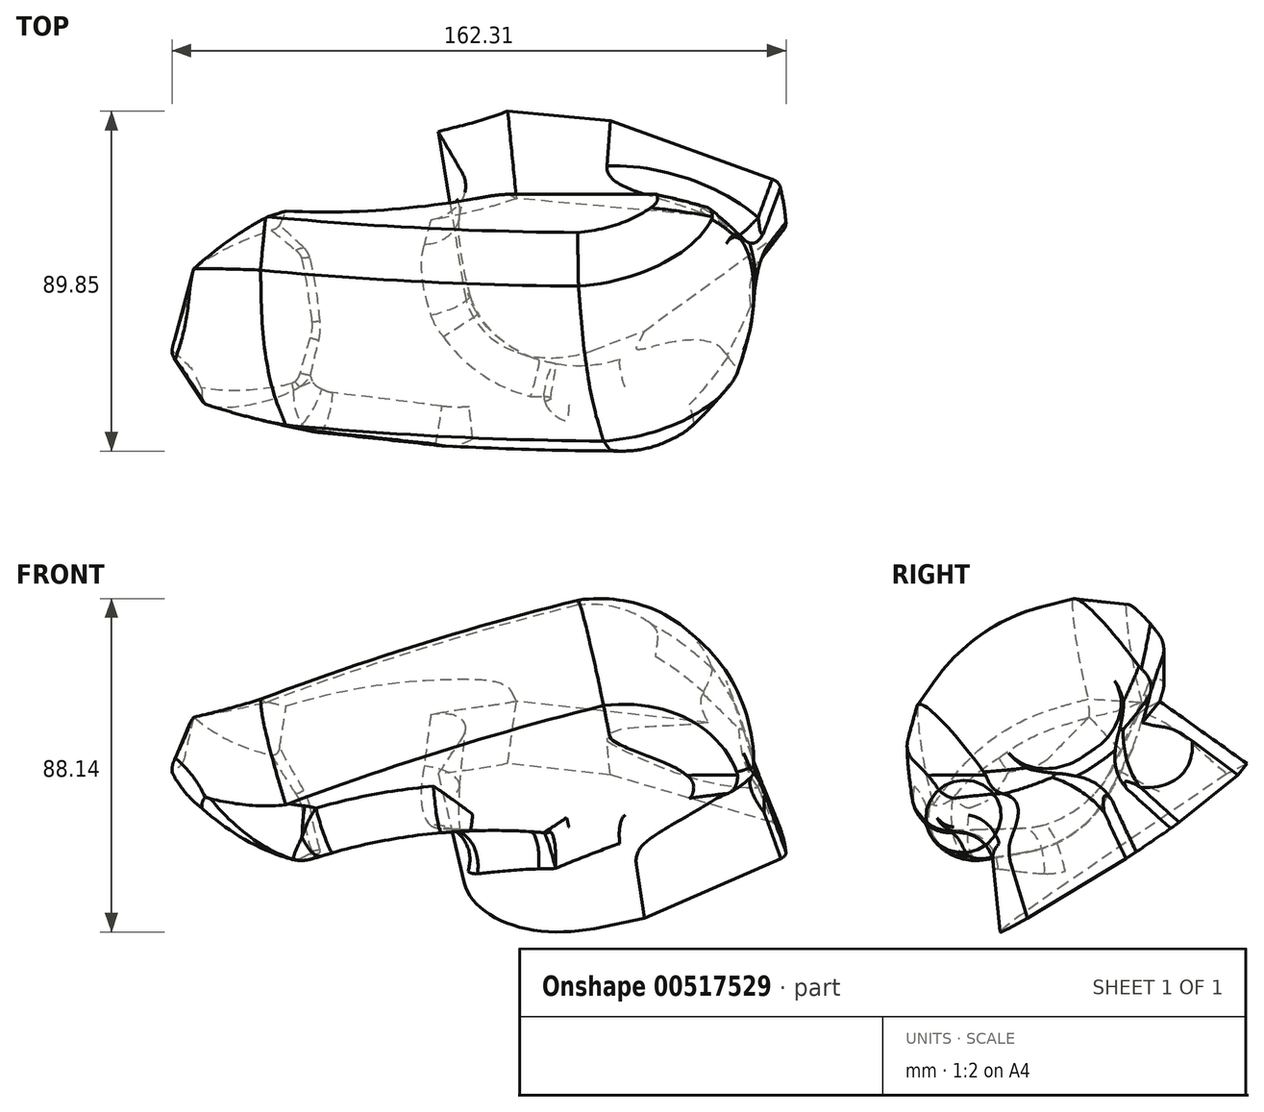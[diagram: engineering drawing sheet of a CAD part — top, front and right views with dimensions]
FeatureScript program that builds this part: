
annotation { "Feature Type Name" : "Feature", "Feature Type Description" : "" }
export const myFeature = defineFeature(function(context is Context, id is Id, definition is map)
    precondition{}
    {
        {
            var Q0;
            Q0=qCreatedBy(makeId("Front.planeOp"),FACE);
            var sketch = newSketch(context, id + "F0", { "sketchPlane" : qUnion([Q0])});
            skArc(sketch, "E0", {"start": v(39.04, 44.79) * mm, "mid": v(-4.05, 32.33) * mm, "end": v(-46.15, 16.82) * mm});
            skArc(sketch, "E1", {"start": v(-36.76, -19.76) * mm, "mid": v(-31.27, -20.86) * mm, "end": v(-25.67, -21) * mm});
            skArc(sketch, "E2", {"start": v(17.25, -16.9) * mm, "mid": v(-4.42, -16.77) * mm, "end": v(-25.67, -21) * mm});
            skArc(sketch, "E3", {"start": v(-68, -2) * mm, "mid": v(-48.8, -15.86) * mm, "end": v(-25.67, -21) * mm});
            skArc(sketch, "E4", {"start": v(88.24, 0) * mm, "mid": v(73.95, 33.71) * mm, "end": v(39.04, 44.79) * mm});
            skArc(sketch, "E5", {"start": v(88.24, 0) * mm, "mid": v(86.09, -26.94) * mm, "end": v(88.24, -53.88) * mm});
            skArc(sketch, "E6", {"start": v(25.94, -54.42) * mm, "mid": v(26.86, -34.44) * mm, "end": v(17.25, -16.9) * mm});
            skLineSegment(sketch, "E7", {"start": v(25.94, -54.42) * mm, "end": v(88.24, -53.88) * mm});
            skArc(sketch, "E8", {"start": v(89.31, 54.42) * mm, "mid": v(62.07, 56.05) * mm, "end": v(43.59, 35.97) * mm, "construction": true});
            skArc(sketch, "E9", {"start": v(75.94, 13.5) * mm, "mid": v(92.5, 30.73) * mm, "end": v(89.31, 54.42) * mm, "construction": true});
            skArc(sketch, "E10", {"start": v(75.94, 13.5) * mm, "mid": v(62.88, 29.22) * mm, "end": v(43.59, 35.97) * mm, "construction": true});
            skLineSegment(sketch, "E11", {"start": v(17.25, -16.9) * mm, "end": v(88.24, 0) * mm});
            skPoint(sketch, "E12.orphan", {"position": v(-57.22, -2) * mm});
            skArc(sketch, "E13", {"start": v(-66.55, 11.44) * mm, "mid": v(-69.79, 4.99) * mm, "end": v(-68, -2) * mm});
            skArc(sketch, "E14", {"start": v(-66.55, 11.44) * mm, "mid": v(-56.28, 13.86) * mm, "end": v(-46.15, 16.82) * mm});
            skPoint(sketch, "E15.orphan", {"position": v(-57.22, 12.17) * mm});
            skPoint(sketch, "E16.start.orphan", {"position": v(-73.67, 12.17) * mm});
            skSolve(sketch);
        }
        {
            var Q0;
            Q0=makeQuery(id+"F0.imprint","IMPRINT",FACE,{"disambiguationData":[TD([[makeQuery(id+"F0.imprint","IMPRINT",EDGE,{"derivedFrom":sQuery(id+"F0.wireOp",EDGE,"E0")}),1.0]])]});
            extrude(context, id + "F1", {"entities" : qUnion([Q0]), "depth" : 25 * mm, "offsetDistance" : 25 * mm, "hasDraft" : true, "draftAngle" : 20 * degree, "draftPullDirection" : true});
        }
        {
            var Q0;
            Q0=makeQuery(id+"F1.opExtrude","CAP_FACE",FACE,{"disambiguationData":[OSD([sQuery(id+"F0.wireOp",EDGE,"E0"),sQuery(id+"F0.wireOp",EDGE,"p0q2MJaU-Hp2x-FXpI-a7RR-1GAnmMj39aOJ"),sQuery(id+"F0.wireOp",EDGE,"E2"),sQuery(id+"F0.wireOp",EDGE,"1ELn8xg3-YaXG-rdAX-tHKt-Tl8SfEgkcqDu"),sQuery(id+"F0.wireOp",EDGE,"E3"),sQuery(id+"F0.wireOp",EDGE,"E4"),sQuery(id+"F0.wireOp",EDGE,"E11")])],"isStart":false});
            extrude(context, id + "F2", {"entities" : qUnion([Q0]), "operationType" : NewBodyOperationType.ADD, "depth" : 10.9 * mm, "offsetDistance" : 25 * mm, "hasDraft" : true, "draftAngle" : 40 * degree, "draftPullDirection" : true});
        }
        {
            var Q0;
            Q0=makeQuery(id+"F1.opExtrude","CAP_FACE",FACE,{"disambiguationData":[OSD([sQuery(id+"F0.wireOp",EDGE,"E0"),sQuery(id+"F0.wireOp",EDGE,"p0q2MJaU-Hp2x-FXpI-a7RR-1GAnmMj39aOJ"),sQuery(id+"F0.wireOp",EDGE,"E2"),sQuery(id+"F0.wireOp",EDGE,"1ELn8xg3-YaXG-rdAX-tHKt-Tl8SfEgkcqDu"),sQuery(id+"F0.wireOp",EDGE,"E3"),sQuery(id+"F0.wireOp",EDGE,"E4"),sQuery(id+"F0.wireOp",EDGE,"E11")])],"isStart":true});
            var sketch = newSketch(context, id + "F3", { "sketchPlane" : qUnion([Q0])});
            skArc(sketch, "E17", {"start": v(-39.04, 44.79) * mm, "mid": v(-14, -32.04) * mm, "end": v(62.82, -7) * mm});
            skSolve(sketch);
        }
        {
            var Q0;
            Q0 = qSketchRegion(id + "F3", true);
            var Q1;
            {var subQ0=sQuery(id+"F3.wireOp",EDGE,"E17");Q1=makeQuery(id+"F3.imprint","IMPRINT",FACE,{"disambiguationData":[TD([[makeQuery(id+"F3.imprint","IMPRINT",EDGE,{"derivedFrom":subQ0}),1.0]])]});}
            extrude(context, id + "F4", {"entities" : qUnion([Q0, Q1]), "operationType" : NewBodyOperationType.REMOVE, "oppositeDirection" : true, "depth" : 25 * mm, "offsetDistance" : 25 * mm});
        }
        {
            var Q0;
            Q0=makeQuery(id+"F1.opExtrude","CAP_FACE",FACE,{"disambiguationData":[OSD([sQuery(id+"F0.wireOp",EDGE,"E0"),sQuery(id+"F0.wireOp",EDGE,"p0q2MJaU-Hp2x-FXpI-a7RR-1GAnmMj39aOJ"),sQuery(id+"F0.wireOp",EDGE,"E2"),sQuery(id+"F0.wireOp",EDGE,"1ELn8xg3-YaXG-rdAX-tHKt-Tl8SfEgkcqDu"),sQuery(id+"F0.wireOp",EDGE,"E3"),sQuery(id+"F0.wireOp",EDGE,"E4"),sQuery(id+"F0.wireOp",EDGE,"E11")])],"isStart":true});
            var sketch = newSketch(context, id + "F5", { "sketchPlane" : qUnion([Q0])});
            skLineSegment(sketch, "E18", {"start": v(-17.25, -16.9) * mm, "end": v(-17.25, 0) * mm});
            skLineSegment(sketch, "E19", {"start": v(-17.25, 0) * mm, "end": v(-88.24, 0) * mm});
            skSolve(sketch);
        }
        {
            var Q0;
            Q0 = qSketchRegion(id + "F5", true);
            var Q1;
            Q1=makeQuery(id+"F5.imprint","IMPRINT",FACE,{"disambiguationData":[TD([[makeQuery(id+"F5.imprint","IMPRINT",EDGE,{"derivedFrom":sQuery(id+"F5.wireOp",EDGE,"E18")}),1.0]])]});
            extrude(context, id + "F6", {"entities" : qUnion([Q0, Q1]), "operationType" : NewBodyOperationType.REMOVE, "oppositeDirection" : true, "depth" : 76.9 * mm, "offsetDistance" : 25 * mm});
        }
        {
            var Q0;
            {var subQ0=sQuery(id+"F0.wireOp",EDGE,"E2");Q0=makeQuery(id+"F2.boolean.opBoolean","MERGE",EDGE,{"derivedFrom":[makeQuery(id+"F1.opExtrude","CAP_EDGE",EDGE,{"disambiguationData":[OSD([subQ0])],"isStart":false}),makeQuery(id+"F2.opExtrude","CAP_EDGE",EDGE,{"disambiguationData":[OSD([subQ0])],"isStart":true})]});}
            fillet(context, id + "F7", {"entities" : qUnion([Q0]), "radius" : 363 * mm, "tangentPropagation" : true, "allowEdgeOverflow" : false});
        }
        {
            var Q0;
            Q0=makeQuery(id+"F1.opExtrude","SWEPT_BODY",BODY,{"disambiguationData":[OSD([sQuery(id+"F0.wireOp",EDGE,"E0"),sQuery(id+"F0.wireOp",EDGE,"p0q2MJaU-Hp2x-FXpI-a7RR-1GAnmMj39aOJ"),sQuery(id+"F0.wireOp",EDGE,"E2"),sQuery(id+"F0.wireOp",EDGE,"1ELn8xg3-YaXG-rdAX-tHKt-Tl8SfEgkcqDu"),sQuery(id+"F0.wireOp",EDGE,"E3"),sQuery(id+"F0.wireOp",EDGE,"E4"),sQuery(id+"F0.wireOp",EDGE,"E11")])]});
            var Q1;
            Q1=qCreatedBy(makeId("Front.planeOp"),FACE);
            mirror(context, id + "F8", {"operationType" : NewBodyOperationType.ADD, "entities" : qUnion([Q0]), "mirrorPlane" : qUnion([Q1])});
        }
        {
            var Q0;
            {var subQ0=makeQuery(id+"F1.opExtrude","CAP_EDGE",EDGE,{"disambiguationData":[OSD([sQuery(id+"F0.wireOp",EDGE,"E0")])],"isStart":true});Q0=makeQuery(id+"F8.boolean.opBoolean","MERGE",EDGE,{"derivedFrom":[subQ0,makeQuery(id+"F8.opPattern","COPY",EDGE,{"derivedFrom":subQ0,"instanceName":"1"})]});}
            var Q1;
            {var subQ0=makeQuery(id+"F1.opExtrude","CAP_EDGE",EDGE,{"disambiguationData":[OSD([sQuery(id+"F0.wireOp",EDGE,"E4")])],"isStart":true});Q1=makeQuery(id+"F8.boolean.opBoolean","MERGE",EDGE,{"derivedFrom":[subQ0,makeQuery(id+"F8.opPattern","COPY",EDGE,{"derivedFrom":subQ0,"instanceName":"1"})]});}
            fillet(context, id + "F9", {"entities" : qUnion([Q0, Q1]), "radius" : 50 * mm, "tangentPropagation" : true, "allowEdgeOverflow" : false});
        }
        {
            var Q0;
            Q0=makeQuery(id+"F2.opExtrude","CAP_EDGE",EDGE,{"disambiguationData":[OSD([sQuery(id+"F0.wireOp",EDGE,"E3")])],"isStart":false});
            fillet(context, id + "F10", {"entities" : qUnion([Q0]), "radius" : 10 * mm, "tangentPropagation" : true, "allowEdgeOverflow" : false});
        }
        {
            var Q0;
            Q0=makeQuery(id+"F10.opFillet","BLEND_EDGE",EDGE,{"blendedFrom":[makeQuery(id+"F2.opExtrude","CAP_EDGE",EDGE,{"disambiguationData":[OSD([sQuery(id+"F0.wireOp",EDGE,"E3")])],"isStart":false}),makeQuery(id+"F2.opExtrude","SWEPT_FACE",FACE,{"disambiguationData":[OSD([sQuery(id+"F0.wireOp",EDGE,"E0")])]})],"blendedInto":[makeQuery(id+"F2.opExtrude","SWEPT_FACE",FACE,{"disambiguationData":[OSD([sQuery(id+"F0.wireOp",EDGE,"E0")])]})]});
            var Q1;
            Q1=makeQuery(id+"F10.opFillet","BLEND_EDGE",EDGE,{"blendedFrom":[makeQuery(id+"F2.opExtrude","CAP_EDGE",EDGE,{"disambiguationData":[OSD([sQuery(id+"F0.wireOp",EDGE,"E3")])],"isStart":false}),makeQuery(id+"F2.opExtrude","SWEPT_FACE",FACE,{"disambiguationData":[OSD([sQuery(id+"F0.wireOp",EDGE,"E14")])]})],"blendedInto":[makeQuery(id+"F2.opExtrude","SWEPT_FACE",FACE,{"disambiguationData":[OSD([sQuery(id+"F0.wireOp",EDGE,"E14")])]})]});
            fillet(context, id + "F11", {"entities" : qUnion([Q0, Q1]), "radius" : 12.2 * mm, "tangentPropagation" : true, "allowEdgeOverflow" : false});
        }
        {
            var Q0;
            {var subQ0=sQuery(id+"F0.wireOp",EDGE,"E2");Q0=makeQuery(id+"F7.opFillet","BLEND_EDGE",EDGE,{"blendedFrom":[makeQuery(id+"F2.boolean.opBoolean","MERGE",EDGE,{"derivedFrom":[makeQuery(id+"F1.opExtrude","CAP_EDGE",EDGE,{"disambiguationData":[OSD([subQ0])],"isStart":false}),makeQuery(id+"F2.opExtrude","CAP_EDGE",EDGE,{"disambiguationData":[OSD([subQ0])],"isStart":true})]}),makeQuery(id+"F2.opExtrude","SWEPT_FACE",FACE,{"disambiguationData":[OSD([sQuery(id+"F0.wireOp",EDGE,"E3")])]})],"blendedInto":[makeQuery(id+"F2.opExtrude","SWEPT_FACE",FACE,{"disambiguationData":[OSD([sQuery(id+"F0.wireOp",EDGE,"E3")])]})]});}
            var Q1;
            Q1=makeQuery(id+"F11.opFillet","BLEND_EDGE",EDGE,{"disambiguationData":[OD(1.0)],"blendedFrom":[makeQuery(id+"F2.opExtrude","SWEPT_EDGE",EDGE,{"disambiguationData":[OSD([sQuery(id+"F0.wireOp",EDGE,"E3"),sQuery(id+"F0.wireOp",EDGE,"E14")])]}),makeQuery(id+"F7.opFillet","BLEND_FACE",FACE,{"disambiguationData":[OSD([sQuery(id+"F0.wireOp",EDGE,"E2")])]})],"blendedInto":[makeQuery(id+"F7.opFillet","BLEND_FACE",FACE,{"disambiguationData":[OSD([sQuery(id+"F0.wireOp",EDGE,"E2")])]})]});
            fillet(context, id + "F12", {"entities" : qUnion([Q0, Q1]), "radius" : 10 * mm, "tangentPropagation" : true, "allowEdgeOverflow" : false});
        }
        {
            var Q0;
            {var subQ0=makeQuery(id+"F1.opExtrude","CAP_EDGE",EDGE,{"disambiguationData":[OSD([sQuery(id+"F0.wireOp",EDGE,"E3")])],"isStart":true});Q0=makeQuery(id+"F8.boolean.opBoolean","MERGE",EDGE,{"derivedFrom":[subQ0,makeQuery(id+"F8.opPattern","COPY",EDGE,{"derivedFrom":subQ0,"instanceName":"1"})]});}
            var Q1;
            {var subQ0=sQuery(id+"F0.wireOp",EDGE,"E2");var subQ1=makeQuery(id+"F7.opFillet","BLEND_EDGE",EDGE,{"blendedFrom":[makeQuery(id+"F2.boolean.opBoolean","MERGE",EDGE,{"derivedFrom":[makeQuery(id+"F1.opExtrude","CAP_EDGE",EDGE,{"disambiguationData":[OSD([subQ0])],"isStart":false}),makeQuery(id+"F2.opExtrude","CAP_EDGE",EDGE,{"disambiguationData":[OSD([subQ0])],"isStart":true})]}),makeQuery(id+"F1.opExtrude","CAP_FACE",FACE,{"disambiguationData":[OSD([sQuery(id+"F0.wireOp",EDGE,"E0"),subQ0,sQuery(id+"F0.wireOp",EDGE,"E3"),sQuery(id+"F0.wireOp",EDGE,"E4"),sQuery(id+"F0.wireOp",EDGE,"E11"),sQuery(id+"F0.wireOp",EDGE,"E13"),sQuery(id+"F0.wireOp",EDGE,"E14")])],"isStart":true})],"blendedInto":[makeQuery(id+"F1.opExtrude","CAP_FACE",FACE,{"disambiguationData":[OSD([sQuery(id+"F0.wireOp",EDGE,"E0"),subQ0,sQuery(id+"F0.wireOp",EDGE,"E3"),sQuery(id+"F0.wireOp",EDGE,"E4"),sQuery(id+"F0.wireOp",EDGE,"E11"),sQuery(id+"F0.wireOp",EDGE,"E13"),sQuery(id+"F0.wireOp",EDGE,"E14")])],"isStart":true})]});Q1=makeQuery(id+"F8.boolean.opBoolean","MERGE",EDGE,{"derivedFrom":[subQ1,makeQuery(id+"F8.opPattern","COPY",EDGE,{"derivedFrom":subQ1,"instanceName":"1"})]});}
            fillet(context, id + "F13", {"entities" : qUnion([Q0, Q1]), "radius" : 30 * mm, "tangentPropagation" : true, "allowEdgeOverflow" : false});
        }
        {
            var Q0;
            {var subQ0=sQuery(id+"F0.wireOp",EDGE,"E3");var subQ1=sQuery(id+"F0.wireOp",EDGE,"E2");var subQ2=makeQuery(id+"F7.opFillet","BLEND_EDGE",EDGE,{"blendedFrom":[makeQuery(id+"F2.boolean.opBoolean","MERGE",EDGE,{"derivedFrom":[makeQuery(id+"F1.opExtrude","CAP_EDGE",EDGE,{"disambiguationData":[OSD([subQ1])],"isStart":false}),makeQuery(id+"F2.opExtrude","CAP_EDGE",EDGE,{"disambiguationData":[OSD([subQ1])],"isStart":true})]}),makeQuery(id+"F1.opExtrude","CAP_FACE",FACE,{"disambiguationData":[OSD([sQuery(id+"F0.wireOp",EDGE,"E0"),subQ1,subQ0,sQuery(id+"F0.wireOp",EDGE,"E4"),sQuery(id+"F0.wireOp",EDGE,"E11"),sQuery(id+"F0.wireOp",EDGE,"E13"),sQuery(id+"F0.wireOp",EDGE,"E14")])],"isStart":true})],"blendedInto":[makeQuery(id+"F1.opExtrude","CAP_FACE",FACE,{"disambiguationData":[OSD([sQuery(id+"F0.wireOp",EDGE,"E0"),subQ1,subQ0,sQuery(id+"F0.wireOp",EDGE,"E4"),sQuery(id+"F0.wireOp",EDGE,"E11"),sQuery(id+"F0.wireOp",EDGE,"E13"),sQuery(id+"F0.wireOp",EDGE,"E14")])],"isStart":true})]});var subQ3=makeQuery(id+"F1.opExtrude","CAP_EDGE",EDGE,{"disambiguationData":[OSD([subQ0])],"isStart":true});Q0=makeQuery(id+"F13.opFillet","BLEND_EDGE",EDGE,{"blendedFrom":[makeQuery(id+"F8.boolean.opBoolean","MERGE",EDGE,{"derivedFrom":[subQ3,makeQuery(id+"F8.opPattern","COPY",EDGE,{"derivedFrom":subQ3,"instanceName":"1"})]}),makeQuery(id+"F8.boolean.opBoolean","MERGE",EDGE,{"derivedFrom":[subQ2,makeQuery(id+"F8.opPattern","COPY",EDGE,{"derivedFrom":subQ2,"instanceName":"1"})]})],"blendedInto":[]});}
            fillet(context, id + "F14", {"entities" : qUnion([Q0]), "radius" : 5 * mm, "tangentPropagation" : true, "allowEdgeOverflow" : false});
        }
        {
            var Q0;
            {var subQ0=makeQuery(id+"F6.boolean.opBoolean","COPY",FACE,{"derivedFrom":makeQuery(id+"F6.opExtrude","SWEPT_FACE",FACE,{"disambiguationData":[OSD([sQuery(id+"F5.wireOp",EDGE,"E19")])]})});Q0=makeQuery(id+"F8.boolean.opBoolean","MERGE",FACE,{"derivedFrom":[subQ0,makeQuery(id+"F8.opPattern","COPY",FACE,{"derivedFrom":subQ0,"instanceName":"1"})]});}
            extrude(context, id + "F15", {"entities" : qUnion([Q0]), "operationType" : NewBodyOperationType.ADD, "depth" : 26.6 * mm, "offsetDistance" : 25 * mm, "hasDraft" : true, "draftAngle" : 20 * degree});
        }
        {
            var Q0;
            {var subQ0=sQuery(id+"F5.wireOp",EDGE,"E19");var subQ1=sQuery(id+"F5.wireOp",EDGE,"E18");var subQ2=sQuery(id+"F0.wireOp",EDGE,"E2");Q0=makeQuery(id+"F15.opExtrude","SWEPT_EDGE",EDGE,{"disambiguationData":[OSD([subQ2,subQ1,subQ0]),TDD([makeQuery(id+"F7.opFillet","BLEND_VERTEX",VERTEX,{"blendedFrom":[makeQuery(id+"F2.boolean.opBoolean","MERGE",EDGE,{"derivedFrom":[makeQuery(id+"F1.opExtrude","CAP_EDGE",EDGE,{"disambiguationData":[OSD([subQ2])],"isStart":false}),makeQuery(id+"F2.opExtrude","CAP_EDGE",EDGE,{"disambiguationData":[OSD([subQ2])],"isStart":true})]}),makeQuery(id+"F6.boolean.opBoolean","COPY",FACE,{"derivedFrom":makeQuery(id+"F6.opExtrude","SWEPT_FACE",FACE,{"disambiguationData":[OSD([subQ1])]})}),makeQuery(id+"F6.boolean.opBoolean","COPY",FACE,{"derivedFrom":makeQuery(id+"F6.opExtrude","SWEPT_FACE",FACE,{"disambiguationData":[OSD([subQ0])]})})],"blendedInto":[makeQuery(id+"F6.boolean.opBoolean","COPY",FACE,{"derivedFrom":makeQuery(id+"F6.opExtrude","SWEPT_FACE",FACE,{"disambiguationData":[OSD([subQ1])]})}),makeQuery(id+"F6.boolean.opBoolean","COPY",FACE,{"derivedFrom":makeQuery(id+"F6.opExtrude","SWEPT_FACE",FACE,{"disambiguationData":[OSD([subQ0])]})})]})])]});}
            fillet(context, id + "F16", {"entities" : qUnion([Q0]), "radius" : 27.28 * mm, "tangentPropagation" : true, "allowEdgeOverflow" : false});
        }
        {
            var Q0;
            {var subQ0=sQuery(id+"F5.wireOp",EDGE,"E19");var subQ1=makeQuery(id+"F6.opExtrude","SWEPT_FACE",FACE,{"disambiguationData":[OSD([subQ0])]});var subQ2=sQuery(id+"F0.wireOp",EDGE,"E11");var subQ3=sQuery(id+"F5.wireOp",EDGE,"E18");var subQ4=sQuery(id+"F0.wireOp",EDGE,"E2");Q0=makeQuery(id+"F16.opFillet","BLEND_EDGE",EDGE,{"blendedFrom":[makeQuery(id+"F15.opExtrude","SWEPT_EDGE",EDGE,{"disambiguationData":[OSD([subQ4,subQ3,subQ0]),TDD([makeQuery(id+"F7.opFillet","BLEND_VERTEX",VERTEX,{"blendedFrom":[makeQuery(id+"F2.boolean.opBoolean","MERGE",EDGE,{"derivedFrom":[makeQuery(id+"F1.opExtrude","CAP_EDGE",EDGE,{"disambiguationData":[OSD([subQ4])],"isStart":false}),makeQuery(id+"F2.opExtrude","CAP_EDGE",EDGE,{"disambiguationData":[OSD([subQ4])],"isStart":true})]}),makeQuery(id+"F6.boolean.opBoolean","COPY",FACE,{"derivedFrom":makeQuery(id+"F6.opExtrude","SWEPT_FACE",FACE,{"disambiguationData":[OSD([subQ3])]})}),makeQuery(id+"F6.boolean.opBoolean","COPY",FACE,{"derivedFrom":subQ1})],"blendedInto":[makeQuery(id+"F6.boolean.opBoolean","COPY",FACE,{"derivedFrom":makeQuery(id+"F6.opExtrude","SWEPT_FACE",FACE,{"disambiguationData":[OSD([subQ3])]})}),makeQuery(id+"F6.boolean.opBoolean","COPY",FACE,{"derivedFrom":subQ1})]})])]}),makeQuery(id+"F15.opExtrude","SWEPT_FACE",FACE,{"disambiguationData":[OSD([subQ2,subQ0]),TDD([makeQuery(id+"F6.boolean.opBoolean","INTERSECT",EDGE,{"derivedFrom":[makeQuery(id+"F2.opExtrude","SWEPT_FACE",FACE,{"disambiguationData":[OSD([subQ2])]}),subQ1]})])]})],"blendedInto":[makeQuery(id+"F15.opExtrude","SWEPT_FACE",FACE,{"disambiguationData":[OSD([subQ2,subQ0]),TDD([makeQuery(id+"F6.boolean.opBoolean","INTERSECT",EDGE,{"derivedFrom":[makeQuery(id+"F2.opExtrude","SWEPT_FACE",FACE,{"disambiguationData":[OSD([subQ2])]}),subQ1]})])]})]});}
            fillet(context, id + "F17", {"entities" : qUnion([Q0]), "radius" : 26.35 * mm, "tangentPropagation" : true, "allowEdgeOverflow" : false});
        }
        {
            var Q0;
            {var subQ0=sQuery(id+"F5.wireOp",EDGE,"E19");var subQ1=makeQuery(id+"F6.opExtrude","SWEPT_FACE",FACE,{"disambiguationData":[OSD([subQ0])]});var subQ2=makeQuery(id+"F6.boolean.opBoolean","COPY",FACE,{"derivedFrom":subQ1});var subQ3=sQuery(id+"F0.wireOp",EDGE,"E11");var subQ4=sQuery(id+"F0.wireOp",EDGE,"E4");var subQ5=makeQuery(id+"F1.opExtrude","CAP_EDGE",EDGE,{"disambiguationData":[OSD([subQ4])],"isStart":true});Q0=makeQuery(id+"F15.opExtrude","SWEPT_EDGE",EDGE,{"disambiguationData":[OSD([subQ4,subQ3,subQ0]),TDD([makeQuery(id+"F9.opFillet","BLEND_VERTEX",VERTEX,{"blendedFrom":[makeQuery(id+"F8.boolean.opBoolean","MERGE",EDGE,{"derivedFrom":[subQ5,makeQuery(id+"F8.opPattern","COPY",EDGE,{"derivedFrom":subQ5,"instanceName":"1"})]}),makeQuery(id+"F6.boolean.opBoolean","SPLIT",FACE,{"disambiguationData":[TD([makeQuery(id+"F1.opExtrude","SWEPT_FACE",FACE,{"disambiguationData":[OSD([subQ4])]})])],"derivedFrom":makeQuery(id+"F1.opExtrude","SWEPT_FACE",FACE,{"disambiguationData":[OSD([subQ3])]})}),makeQuery(id+"F8.boolean.opBoolean","MERGE",FACE,{"derivedFrom":[subQ2,makeQuery(id+"F8.opPattern","COPY",FACE,{"derivedFrom":subQ2,"instanceName":"1"})]})],"blendedInto":[makeQuery(id+"F6.boolean.opBoolean","SPLIT",FACE,{"disambiguationData":[TD([makeQuery(id+"F1.opExtrude","SWEPT_FACE",FACE,{"disambiguationData":[OSD([subQ4])]})])],"derivedFrom":makeQuery(id+"F1.opExtrude","SWEPT_FACE",FACE,{"disambiguationData":[OSD([subQ3])]})}),makeQuery(id+"F8.boolean.opBoolean","MERGE",FACE,{"derivedFrom":[subQ2,makeQuery(id+"F8.opPattern","COPY",FACE,{"derivedFrom":subQ2,"instanceName":"1"})]})]})])]});}
            var Q1;
            {var subQ0=sQuery(id+"F5.wireOp",EDGE,"E19");var subQ1=makeQuery(id+"F6.opExtrude","SWEPT_FACE",FACE,{"disambiguationData":[OSD([subQ0])]});var subQ2=makeQuery(id+"F6.boolean.opBoolean","COPY",FACE,{"derivedFrom":subQ1});var subQ3=sQuery(id+"F0.wireOp",EDGE,"E11");var subQ4=sQuery(id+"F0.wireOp",EDGE,"E4");var subQ5=makeQuery(id+"F1.opExtrude","CAP_EDGE",EDGE,{"disambiguationData":[OSD([subQ4])],"isStart":true});Q1=makeQuery(id+"F15.opExtrude","SWEPT_EDGE",EDGE,{"disambiguationData":[OSD([subQ4,subQ3,subQ0]),TDD([makeQuery(id+"F9.opFillet","BLEND_VERTEX",VERTEX,{"blendedFrom":[makeQuery(id+"F8.boolean.opBoolean","MERGE",EDGE,{"derivedFrom":[subQ5,makeQuery(id+"F8.opPattern","COPY",EDGE,{"derivedFrom":subQ5,"instanceName":"1"})]}),makeQuery(id+"F8.opPattern","COPY",FACE,{"derivedFrom":makeQuery(id+"F6.boolean.opBoolean","SPLIT",FACE,{"disambiguationData":[TD([makeQuery(id+"F1.opExtrude","SWEPT_FACE",FACE,{"disambiguationData":[OSD([subQ4])]})])],"derivedFrom":makeQuery(id+"F1.opExtrude","SWEPT_FACE",FACE,{"disambiguationData":[OSD([subQ3])]})}),"instanceName":"1"}),makeQuery(id+"F8.boolean.opBoolean","MERGE",FACE,{"derivedFrom":[subQ2,makeQuery(id+"F8.opPattern","COPY",FACE,{"derivedFrom":subQ2,"instanceName":"1"})]})],"blendedInto":[makeQuery(id+"F8.opPattern","COPY",FACE,{"derivedFrom":makeQuery(id+"F6.boolean.opBoolean","SPLIT",FACE,{"disambiguationData":[TD([makeQuery(id+"F1.opExtrude","SWEPT_FACE",FACE,{"disambiguationData":[OSD([subQ4])]})])],"derivedFrom":makeQuery(id+"F1.opExtrude","SWEPT_FACE",FACE,{"disambiguationData":[OSD([subQ3])]})}),"instanceName":"1"}),makeQuery(id+"F8.boolean.opBoolean","MERGE",FACE,{"derivedFrom":[subQ2,makeQuery(id+"F8.opPattern","COPY",FACE,{"derivedFrom":subQ2,"instanceName":"1"})]})]})])]});}
            fillet(context, id + "F18", {"entities" : qUnion([Q0, Q1]), "radius" : 4 * mm, "tangentPropagation" : true, "allowEdgeOverflow" : false});
        }
        {
            var Q0;
            {var subQ0=sQuery(id+"F5.wireOp",EDGE,"E19");var subQ1=sQuery(id+"F0.wireOp",EDGE,"E11");var subQ2=makeQuery(id+"F6.boolean.opBoolean","INTERSECT",EDGE,{"derivedFrom":[makeQuery(id+"F1.opExtrude","SWEPT_FACE",FACE,{"disambiguationData":[OSD([subQ1])]}),makeQuery(id+"F6.opExtrude","SWEPT_FACE",FACE,{"disambiguationData":[OSD([subQ0])]})]});Q0=makeQuery(id+"F15.boolean.opBoolean","MERGE",EDGE,{"derivedFrom":[subQ2,makeQuery(id+"F15.opExtrude","CAP_EDGE",EDGE,{"disambiguationData":[OSD([subQ1,subQ0]),TDD([subQ2])],"isStart":true})]});}
            var Q1;
            {var subQ0=sQuery(id+"F5.wireOp",EDGE,"E19");var subQ1=sQuery(id+"F0.wireOp",EDGE,"E11");var subQ2=makeQuery(id+"F8.opPattern","COPY",EDGE,{"derivedFrom":makeQuery(id+"F6.boolean.opBoolean","INTERSECT",EDGE,{"derivedFrom":[makeQuery(id+"F1.opExtrude","SWEPT_FACE",FACE,{"disambiguationData":[OSD([subQ1])]}),makeQuery(id+"F6.opExtrude","SWEPT_FACE",FACE,{"disambiguationData":[OSD([subQ0])]})]}),"instanceName":"1"});Q1=makeQuery(id+"F15.boolean.opBoolean","MERGE",EDGE,{"derivedFrom":[subQ2,makeQuery(id+"F15.opExtrude","CAP_EDGE",EDGE,{"disambiguationData":[OSD([subQ1,subQ0]),TDD([subQ2])],"isStart":true})]});}
            fillet(context, id + "F19", {"entities" : qUnion([Q0, Q1]), "radius" : 20 * mm, "tangentPropagation" : true, "allowEdgeOverflow" : false});
        }
        {
            var Q0;
            {var subQ0=sQuery(id+"F5.wireOp",EDGE,"E19");var subQ1=sQuery(id+"F0.wireOp",EDGE,"E11");var subQ2=makeQuery(id+"F6.boolean.opBoolean","INTERSECT",EDGE,{"derivedFrom":[makeQuery(id+"F2.opExtrude","SWEPT_FACE",FACE,{"disambiguationData":[OSD([subQ1])]}),makeQuery(id+"F6.opExtrude","SWEPT_FACE",FACE,{"disambiguationData":[OSD([subQ0])]})]});Q0=makeQuery(id+"F15.boolean.opBoolean","MERGE",EDGE,{"derivedFrom":[subQ2,makeQuery(id+"F15.opExtrude","CAP_EDGE",EDGE,{"disambiguationData":[OSD([subQ1,subQ0]),TDD([subQ2])],"isStart":true})]});}
            var Q1;
            {var subQ0=sQuery(id+"F0.wireOp",EDGE,"E11");var subQ1=makeQuery(id+"F2.opExtrude","SWEPT_FACE",FACE,{"disambiguationData":[OSD([subQ0])]});var subQ2=sQuery(id+"F5.wireOp",EDGE,"E19");var subQ3=makeQuery(id+"F6.opExtrude","SWEPT_FACE",FACE,{"disambiguationData":[OSD([subQ2])]});var subQ4=sQuery(id+"F5.wireOp",EDGE,"E18");var subQ5=sQuery(id+"F0.wireOp",EDGE,"E2");Q1=makeQuery(id+"F17.opFillet","BLEND_EDGE",EDGE,{"blendedFrom":[makeQuery(id+"F16.opFillet","BLEND_EDGE",EDGE,{"blendedFrom":[makeQuery(id+"F15.opExtrude","SWEPT_EDGE",EDGE,{"disambiguationData":[OSD([subQ5,subQ4,subQ2]),TDD([makeQuery(id+"F7.opFillet","BLEND_VERTEX",VERTEX,{"blendedFrom":[makeQuery(id+"F2.boolean.opBoolean","MERGE",EDGE,{"derivedFrom":[makeQuery(id+"F1.opExtrude","CAP_EDGE",EDGE,{"disambiguationData":[OSD([subQ5])],"isStart":false}),makeQuery(id+"F2.opExtrude","CAP_EDGE",EDGE,{"disambiguationData":[OSD([subQ5])],"isStart":true})]}),makeQuery(id+"F6.boolean.opBoolean","COPY",FACE,{"derivedFrom":makeQuery(id+"F6.opExtrude","SWEPT_FACE",FACE,{"disambiguationData":[OSD([subQ4])]})}),makeQuery(id+"F6.boolean.opBoolean","COPY",FACE,{"derivedFrom":subQ3})],"blendedInto":[makeQuery(id+"F6.boolean.opBoolean","COPY",FACE,{"derivedFrom":makeQuery(id+"F6.opExtrude","SWEPT_FACE",FACE,{"disambiguationData":[OSD([subQ4])]})}),makeQuery(id+"F6.boolean.opBoolean","COPY",FACE,{"derivedFrom":subQ3})]})])]}),makeQuery(id+"F15.opExtrude","SWEPT_FACE",FACE,{"disambiguationData":[OSD([subQ0,subQ2]),TDD([makeQuery(id+"F6.boolean.opBoolean","INTERSECT",EDGE,{"derivedFrom":[subQ1,subQ3]})])]})],"blendedInto":[makeQuery(id+"F15.opExtrude","SWEPT_FACE",FACE,{"disambiguationData":[OSD([subQ0,subQ2]),TDD([makeQuery(id+"F6.boolean.opBoolean","INTERSECT",EDGE,{"derivedFrom":[subQ1,subQ3]})])]})]}),subQ1],"blendedInto":[subQ1]});}
            var Q2;
            {var subQ0=sQuery(id+"F0.wireOp",EDGE,"E2");var subQ1=sQuery(id+"F5.wireOp",EDGE,"E19");var subQ2=makeQuery(id+"F6.opExtrude","SWEPT_FACE",FACE,{"disambiguationData":[OSD([subQ1])]});var subQ3=sQuery(id+"F0.wireOp",EDGE,"E11");var subQ4=sQuery(id+"F5.wireOp",EDGE,"E18");Q2=makeQuery(id+"F17.opFillet","BLEND_EDGE",EDGE,{"blendedFrom":[makeQuery(id+"F16.opFillet","BLEND_EDGE",EDGE,{"blendedFrom":[makeQuery(id+"F15.opExtrude","SWEPT_EDGE",EDGE,{"disambiguationData":[OSD([subQ0,subQ4,subQ1]),TDD([makeQuery(id+"F7.opFillet","BLEND_VERTEX",VERTEX,{"blendedFrom":[makeQuery(id+"F2.boolean.opBoolean","MERGE",EDGE,{"derivedFrom":[makeQuery(id+"F1.opExtrude","CAP_EDGE",EDGE,{"disambiguationData":[OSD([subQ0])],"isStart":false}),makeQuery(id+"F2.opExtrude","CAP_EDGE",EDGE,{"disambiguationData":[OSD([subQ0])],"isStart":true})]}),makeQuery(id+"F6.boolean.opBoolean","COPY",FACE,{"derivedFrom":makeQuery(id+"F6.opExtrude","SWEPT_FACE",FACE,{"disambiguationData":[OSD([subQ4])]})}),makeQuery(id+"F6.boolean.opBoolean","COPY",FACE,{"derivedFrom":subQ2})],"blendedInto":[makeQuery(id+"F6.boolean.opBoolean","COPY",FACE,{"derivedFrom":makeQuery(id+"F6.opExtrude","SWEPT_FACE",FACE,{"disambiguationData":[OSD([subQ4])]})}),makeQuery(id+"F6.boolean.opBoolean","COPY",FACE,{"derivedFrom":subQ2})]})])]}),makeQuery(id+"F15.opExtrude","SWEPT_FACE",FACE,{"disambiguationData":[OSD([subQ3,subQ1]),TDD([makeQuery(id+"F6.boolean.opBoolean","INTERSECT",EDGE,{"derivedFrom":[makeQuery(id+"F2.opExtrude","SWEPT_FACE",FACE,{"disambiguationData":[OSD([subQ3])]}),subQ2]})])]})],"blendedInto":[makeQuery(id+"F15.opExtrude","SWEPT_FACE",FACE,{"disambiguationData":[OSD([subQ3,subQ1]),TDD([makeQuery(id+"F6.boolean.opBoolean","INTERSECT",EDGE,{"derivedFrom":[makeQuery(id+"F2.opExtrude","SWEPT_FACE",FACE,{"disambiguationData":[OSD([subQ3])]}),subQ2]})])]})]}),makeQuery(id+"F7.opFillet","BLEND_FACE",FACE,{"disambiguationData":[OSD([subQ0])]})],"blendedInto":[makeQuery(id+"F7.opFillet","BLEND_FACE",FACE,{"disambiguationData":[OSD([subQ0])]})]});}
            fillet(context, id + "F20", {"entities" : qUnion([Q0, Q1, Q2]), "radius" : 10 * mm, "tangentPropagation" : true, "allowEdgeOverflow" : false});
        }
        {
            var Q0;
            {var subQ0=sQuery(id+"F5.wireOp",EDGE,"E19");var subQ1=sQuery(id+"F0.wireOp",EDGE,"E4");var subQ2=makeQuery(id+"F6.boolean.opBoolean","COPY",FACE,{"derivedFrom":makeQuery(id+"F6.opExtrude","SWEPT_FACE",FACE,{"disambiguationData":[OSD([subQ0])]})});var subQ3=makeQuery(id+"F1.opExtrude","CAP_EDGE",EDGE,{"disambiguationData":[OSD([subQ1])],"isStart":true});Q0=makeQuery(id+"F15.boolean.opBoolean","MERGE",EDGE,{"derivedFrom":[makeQuery(id+"F9.opFillet","BLEND_EDGE",EDGE,{"blendedFrom":[makeQuery(id+"F8.boolean.opBoolean","MERGE",EDGE,{"derivedFrom":[subQ3,makeQuery(id+"F8.opPattern","COPY",EDGE,{"derivedFrom":subQ3,"instanceName":"1"})]}),makeQuery(id+"F8.boolean.opBoolean","MERGE",FACE,{"derivedFrom":[subQ2,makeQuery(id+"F8.opPattern","COPY",FACE,{"derivedFrom":subQ2,"instanceName":"1"})]})],"blendedInto":[makeQuery(id+"F8.boolean.opBoolean","MERGE",FACE,{"derivedFrom":[subQ2,makeQuery(id+"F8.opPattern","COPY",FACE,{"derivedFrom":subQ2,"instanceName":"1"})]})]}),makeQuery(id+"F15.opExtrude","CAP_EDGE",EDGE,{"disambiguationData":[OSD([subQ1,subQ0])],"isStart":true})]});}
            var Q1;
            {var subQ0=sQuery(id+"F5.wireOp",EDGE,"E19");var subQ1=makeQuery(id+"F6.opExtrude","SWEPT_FACE",FACE,{"disambiguationData":[OSD([subQ0])]});var subQ2=makeQuery(id+"F6.boolean.opBoolean","COPY",FACE,{"derivedFrom":subQ1});var subQ3=sQuery(id+"F0.wireOp",EDGE,"E11");var subQ4=sQuery(id+"F0.wireOp",EDGE,"E4");var subQ5=makeQuery(id+"F1.opExtrude","CAP_EDGE",EDGE,{"disambiguationData":[OSD([subQ4])],"isStart":true});var subQ6=makeQuery(id+"F9.opFillet","BLEND_VERTEX",VERTEX,{"blendedFrom":[makeQuery(id+"F8.boolean.opBoolean","MERGE",EDGE,{"derivedFrom":[subQ5,makeQuery(id+"F8.opPattern","COPY",EDGE,{"derivedFrom":subQ5,"instanceName":"1"})]}),makeQuery(id+"F8.opPattern","COPY",FACE,{"derivedFrom":makeQuery(id+"F6.boolean.opBoolean","SPLIT",FACE,{"disambiguationData":[TD([makeQuery(id+"F1.opExtrude","SWEPT_FACE",FACE,{"disambiguationData":[OSD([subQ4])]})])],"derivedFrom":makeQuery(id+"F1.opExtrude","SWEPT_FACE",FACE,{"disambiguationData":[OSD([subQ3])]})}),"instanceName":"1"}),makeQuery(id+"F8.boolean.opBoolean","MERGE",FACE,{"derivedFrom":[subQ2,makeQuery(id+"F8.opPattern","COPY",FACE,{"derivedFrom":subQ2,"instanceName":"1"})]})],"blendedInto":[makeQuery(id+"F8.opPattern","COPY",FACE,{"derivedFrom":makeQuery(id+"F6.boolean.opBoolean","SPLIT",FACE,{"disambiguationData":[TD([makeQuery(id+"F1.opExtrude","SWEPT_FACE",FACE,{"disambiguationData":[OSD([subQ4])]})])],"derivedFrom":makeQuery(id+"F1.opExtrude","SWEPT_FACE",FACE,{"disambiguationData":[OSD([subQ3])]})}),"instanceName":"1"}),makeQuery(id+"F8.boolean.opBoolean","MERGE",FACE,{"derivedFrom":[subQ2,makeQuery(id+"F8.opPattern","COPY",FACE,{"derivedFrom":subQ2,"instanceName":"1"})]})]});Q1=makeQuery(id+"F19.opFillet","TWEAK_EDGE",EDGE,{"derivedFrom":[makeQuery(id+"F15.boolean.opBoolean","MERGE",VERTEX,{"derivedFrom":[subQ6,makeQuery(id+"F15.opExtrude","CAP_VERTEX",VERTEX,{"disambiguationData":[OSD([subQ4,subQ3,subQ0]),TDD([subQ6])],"isStart":true})]})]});}
            var Q2;
            {var subQ0=sQuery(id+"F5.wireOp",EDGE,"E19");var subQ1=makeQuery(id+"F6.opExtrude","SWEPT_FACE",FACE,{"disambiguationData":[OSD([subQ0])]});var subQ2=makeQuery(id+"F6.boolean.opBoolean","COPY",FACE,{"derivedFrom":subQ1});var subQ3=sQuery(id+"F0.wireOp",EDGE,"E11");var subQ4=sQuery(id+"F0.wireOp",EDGE,"E4");var subQ5=makeQuery(id+"F1.opExtrude","CAP_EDGE",EDGE,{"disambiguationData":[OSD([subQ4])],"isStart":true});var subQ6=makeQuery(id+"F9.opFillet","BLEND_VERTEX",VERTEX,{"blendedFrom":[makeQuery(id+"F8.boolean.opBoolean","MERGE",EDGE,{"derivedFrom":[subQ5,makeQuery(id+"F8.opPattern","COPY",EDGE,{"derivedFrom":subQ5,"instanceName":"1"})]}),makeQuery(id+"F6.boolean.opBoolean","SPLIT",FACE,{"disambiguationData":[TD([makeQuery(id+"F1.opExtrude","SWEPT_FACE",FACE,{"disambiguationData":[OSD([subQ4])]})])],"derivedFrom":makeQuery(id+"F1.opExtrude","SWEPT_FACE",FACE,{"disambiguationData":[OSD([subQ3])]})}),makeQuery(id+"F8.boolean.opBoolean","MERGE",FACE,{"derivedFrom":[subQ2,makeQuery(id+"F8.opPattern","COPY",FACE,{"derivedFrom":subQ2,"instanceName":"1"})]})],"blendedInto":[makeQuery(id+"F6.boolean.opBoolean","SPLIT",FACE,{"disambiguationData":[TD([makeQuery(id+"F1.opExtrude","SWEPT_FACE",FACE,{"disambiguationData":[OSD([subQ4])]})])],"derivedFrom":makeQuery(id+"F1.opExtrude","SWEPT_FACE",FACE,{"disambiguationData":[OSD([subQ3])]})}),makeQuery(id+"F8.boolean.opBoolean","MERGE",FACE,{"derivedFrom":[subQ2,makeQuery(id+"F8.opPattern","COPY",FACE,{"derivedFrom":subQ2,"instanceName":"1"})]})]});Q2=makeQuery(id+"F19.opFillet","TWEAK_EDGE",EDGE,{"derivedFrom":[makeQuery(id+"F18.opFillet","TWEAK_VERTEX",VERTEX,{"derivedFrom":[makeQuery(id+"F15.boolean.opBoolean","MERGE",VERTEX,{"derivedFrom":[subQ6,makeQuery(id+"F15.opExtrude","CAP_VERTEX",VERTEX,{"disambiguationData":[OSD([subQ4,subQ3,subQ0]),TDD([subQ6])],"isStart":true})]})]})]});}
            fillet(context, id + "F21", {"entities" : qUnion([Q0, Q1, Q2]), "radius" : 11 * mm, "tangentPropagation" : true, "allowEdgeOverflow" : false});
        }
        {
            var Q0;
            Q0=makeQuery(id+"F2.opExtrude","SWEPT_EDGE",EDGE,{"disambiguationData":[OSD([sQuery(id+"F0.wireOp",EDGE,"E4"),sQuery(id+"F0.wireOp",EDGE,"E5"),sQuery(id+"F0.wireOp",EDGE,"E11")])]});
            var Q1;
            {var subQ0=sQuery(id+"F5.wireOp",EDGE,"E19");var subQ1=sQuery(id+"F0.wireOp",EDGE,"E11");var subQ2=makeQuery(id+"F6.boolean.opBoolean","INTERSECT",EDGE,{"derivedFrom":[makeQuery(id+"F1.opExtrude","SWEPT_FACE",FACE,{"disambiguationData":[OSD([subQ1])]}),makeQuery(id+"F6.opExtrude","SWEPT_FACE",FACE,{"disambiguationData":[OSD([subQ0])]})]});Q1=makeQuery(id+"F19.opFillet","BLEND_EDGE",EDGE,{"blendedFrom":[makeQuery(id+"F15.boolean.opBoolean","MERGE",EDGE,{"derivedFrom":[subQ2,makeQuery(id+"F15.opExtrude","CAP_EDGE",EDGE,{"disambiguationData":[OSD([subQ1,subQ0]),TDD([subQ2])],"isStart":true})]}),makeQuery(id+"F1.opExtrude","SWEPT_FACE",FACE,{"disambiguationData":[OSD([sQuery(id+"F0.wireOp",EDGE,"E4")])]})],"blendedInto":[makeQuery(id+"F1.opExtrude","SWEPT_FACE",FACE,{"disambiguationData":[OSD([sQuery(id+"F0.wireOp",EDGE,"E4")])]})]});}
            var Q2;
            {var subQ0=sQuery(id+"F5.wireOp",EDGE,"E19");var subQ1=sQuery(id+"F0.wireOp",EDGE,"E11");var subQ2=makeQuery(id+"F8.opPattern","COPY",EDGE,{"derivedFrom":makeQuery(id+"F6.boolean.opBoolean","INTERSECT",EDGE,{"derivedFrom":[makeQuery(id+"F1.opExtrude","SWEPT_FACE",FACE,{"disambiguationData":[OSD([subQ1])]}),makeQuery(id+"F6.opExtrude","SWEPT_FACE",FACE,{"disambiguationData":[OSD([subQ0])]})]}),"instanceName":"1"});Q2=makeQuery(id+"F19.opFillet","BLEND_EDGE",EDGE,{"blendedFrom":[makeQuery(id+"F15.boolean.opBoolean","MERGE",EDGE,{"derivedFrom":[subQ2,makeQuery(id+"F15.opExtrude","CAP_EDGE",EDGE,{"disambiguationData":[OSD([subQ1,subQ0]),TDD([subQ2])],"isStart":true})]}),makeQuery(id+"F8.opPattern","COPY",FACE,{"derivedFrom":makeQuery(id+"F1.opExtrude","SWEPT_FACE",FACE,{"disambiguationData":[OSD([sQuery(id+"F0.wireOp",EDGE,"E4")])]}),"instanceName":"1"})],"blendedInto":[makeQuery(id+"F8.opPattern","COPY",FACE,{"derivedFrom":makeQuery(id+"F1.opExtrude","SWEPT_FACE",FACE,{"disambiguationData":[OSD([sQuery(id+"F0.wireOp",EDGE,"E4")])]}),"instanceName":"1"})]});}
            var Q3;
            Q3=makeQuery(id+"F8.opPattern","COPY",EDGE,{"derivedFrom":makeQuery(id+"F2.opExtrude","SWEPT_EDGE",EDGE,{"disambiguationData":[OSD([sQuery(id+"F0.wireOp",EDGE,"E4"),sQuery(id+"F0.wireOp",EDGE,"E5"),sQuery(id+"F0.wireOp",EDGE,"E11")])]}),"instanceName":"1"});
            var Q4;
            Q4=makeQuery(id+"F2.opExtrude","CAP_EDGE",EDGE,{"disambiguationData":[OSD([sQuery(id+"F0.wireOp",EDGE,"E11")])],"isStart":false});
            var Q5;
            Q5=makeQuery(id+"F8.opPattern","COPY",EDGE,{"derivedFrom":makeQuery(id+"F2.opExtrude","CAP_EDGE",EDGE,{"disambiguationData":[OSD([sQuery(id+"F0.wireOp",EDGE,"E11")])],"isStart":false}),"instanceName":"1"});
            fillet(context, id + "F22", {"entities" : qUnion([Q0, Q1, Q2, Q3, Q4, Q5]), "radius" : 6 * mm, "tangentPropagation" : true, "allowEdgeOverflow" : false});
        }
        {
            var Q0;
            Q0=makeQuery(id+"F1.opExtrude","SWEPT_BODY",BODY,{"disambiguationData":[OSD([sQuery(id+"F0.wireOp",EDGE,"E0"),sQuery(id+"F0.wireOp",EDGE,"E2"),sQuery(id+"F0.wireOp",EDGE,"E3"),sQuery(id+"F0.wireOp",EDGE,"E4"),sQuery(id+"F0.wireOp",EDGE,"E11"),sQuery(id+"F0.wireOp",EDGE,"E13"),sQuery(id+"F0.wireOp",EDGE,"E14")])]});
            var Q1;
            {var subQ0=sQuery(id+"F0.wireOp",EDGE,"E11");Q1=makeQuery(id+"F22.opFillet","BLEND_EDGE",EDGE,{"blendedFrom":[makeQuery(id+"F2.opExtrude","CAP_EDGE",EDGE,{"disambiguationData":[OSD([subQ0])],"isStart":false}),makeQuery(id+"F2.opExtrude","SWEPT_FACE",FACE,{"disambiguationData":[OSD([subQ0])]})],"blendedInto":[makeQuery(id+"F2.opExtrude","SWEPT_FACE",FACE,{"disambiguationData":[OSD([subQ0])]})]});}
            transform(context, id + "F23", {"entities" : qUnion([Q0]), "transformType" : TransformType.ROTATION, "transformAxis" : qUnion([Q1]), "angle" : 35 * degree, "makeCopy" : false});
        }
        {
            var Q0;
            Q0=makeQuery(id+"F1.opExtrude","SWEPT_BODY",BODY,{"disambiguationData":[OSD([sQuery(id+"F0.wireOp",EDGE,"E0"),sQuery(id+"F0.wireOp",EDGE,"E2"),sQuery(id+"F0.wireOp",EDGE,"E3"),sQuery(id+"F0.wireOp",EDGE,"E4"),sQuery(id+"F0.wireOp",EDGE,"E11"),sQuery(id+"F0.wireOp",EDGE,"E13"),sQuery(id+"F0.wireOp",EDGE,"E14")])]});
            transform(context, id + "F24", {"entities" : qUnion([Q0]), "transformType" : TransformType.TRANSLATION_3D, "dx" : 0 * mm, "dy" : 42.3 * mm, "dz" : 0 * mm, "makeCopy" : false});
        }
    });
